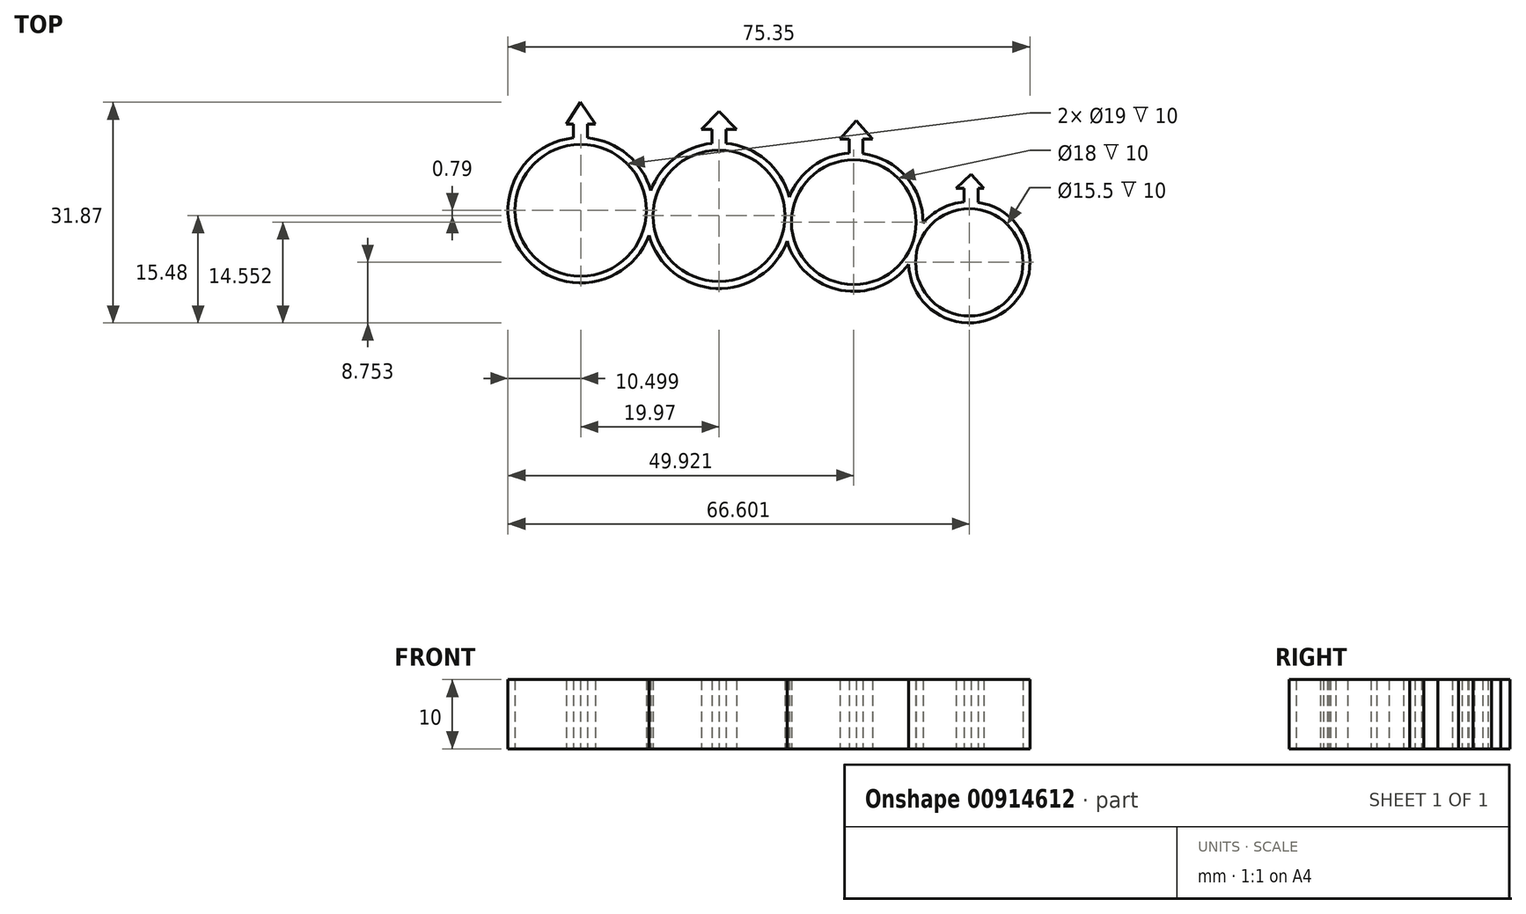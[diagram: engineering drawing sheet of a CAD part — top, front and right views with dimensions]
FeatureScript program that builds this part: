
annotation { "Feature Type Name" : "Feature", "Feature Type Description" : "" }
export const myFeature = defineFeature(function(context is Context, id is Id, definition is map)
    precondition{}
    {
        {
            var Q0;
            Q0=qCreatedBy(makeId("Top.planeOp"),FACE);
            var sketch = newSketch(context, id + "F0", { "sketchPlane" : qUnion([Q0])});
            skCircle(sketch, "E0", {"center": v(-63.63, 34.75) * mm, "radius": 9.5 * mm});
            skCircle(sketch, "E1", {"center": v(-43.66, 33.96) * mm, "radius": 9.5 * mm});
            skCircle(sketch, "E2", {"center": v(-24.2, 33.03) * mm, "radius": 9 * mm});
            skCircle(sketch, "E3", {"center": v(-7.53, 27.23) * mm, "radius": 7.75 * mm});
            skCircle(sketch, "E4", {"center": v(-63.63, 34.75) * mm, "radius": 10.5 * mm});
            skCircle(sketch, "E5", {"center": v(-43.66, 33.96) * mm, "radius": 10.5 * mm});
            skCircle(sketch, "E6", {"center": v(-24.2, 33.03) * mm, "radius": 10 * mm});
            skCircle(sketch, "E7", {"center": v(-7.53, 27.23) * mm, "radius": 8.75 * mm});
            skLineSegment(sketch, "E8", {"start": v(-64.68, 45.2) * mm, "end": v(-64.68, 47.2) * mm});
            skLineSegment(sketch, "E9", {"start": v(-64.68, 47.2) * mm, "end": v(-62.68, 47.2) * mm});
            skLineSegment(sketch, "E10", {"start": v(-62.68, 47.2) * mm, "end": v(-62.68, 45.2) * mm});
            skLineSegment(sketch, "E11", {"start": v(-44.67, 44.41) * mm, "end": v(-44.67, 46.41) * mm});
            skLineSegment(sketch, "E12", {"start": v(-44.67, 46.41) * mm, "end": v(-42.67, 46.41) * mm});
            skLineSegment(sketch, "E13", {"start": v(-42.67, 46.41) * mm, "end": v(-42.67, 44.41) * mm});
            skLineSegment(sketch, "E14", {"start": v(-42.67, 44.41) * mm, "end": v(-42.67, 46.41) * mm});
            skLineSegment(sketch, "E15", {"start": v(-24.87, 43) * mm, "end": v(-24.87, 45) * mm});
            skLineSegment(sketch, "E16", {"start": v(-24.87, 45) * mm, "end": v(-22.87, 45.07) * mm});
            skLineSegment(sketch, "E17", {"start": v(-22.87, 45.07) * mm, "end": v(-22.87, 42.94) * mm});
            skLineSegment(sketch, "E18", {"start": v(-22.87, 42.94) * mm, "end": v(-22.87, 45.07) * mm});
            skLineSegment(sketch, "E19", {"start": v(-8.27, 35.95) * mm, "end": v(-8.27, 37.95) * mm});
            skLineSegment(sketch, "E20", {"start": v(-8.27, 37.95) * mm, "end": v(-6.27, 37.95) * mm});
            skLineSegment(sketch, "E21", {"start": v(-6.27, 37.95) * mm, "end": v(-6.27, 35.9) * mm});
            skLineSegment(sketch, "E22", {"start": v(-64.68, 47.2) * mm, "end": v(-65.72, 47.2) * mm});
            skLineSegment(sketch, "E23", {"start": v(-65.72, 47.2) * mm, "end": v(-63.68, 50.35) * mm});
            skPoint(sketch, "E23.endSnap0", {"position": v(-63.68, 47.2) * mm});
            skLineSegment(sketch, "E24", {"start": v(-63.68, 50.35) * mm, "end": v(-61.49, 47.2) * mm});
            skLineSegment(sketch, "E25", {"start": v(-61.49, 47.2) * mm, "end": v(-62.68, 47.2) * mm});
            skLineSegment(sketch, "E26", {"start": v(-44.67, 46.41) * mm, "end": v(-46.2, 46.41) * mm});
            skLineSegment(sketch, "E27", {"start": v(-46.2, 46.41) * mm, "end": v(-43.67, 49.02) * mm});
            skPoint(sketch, "E27.endSnap0", {"position": v(-43.67, 46.41) * mm});
            skLineSegment(sketch, "E28", {"start": v(-43.67, 49.02) * mm, "end": v(-41.14, 46.41) * mm});
            skLineSegment(sketch, "E29", {"start": v(-41.14, 46.41) * mm, "end": v(-42.67, 46.41) * mm});
            skLineSegment(sketch, "E30", {"start": v(-24.87, 45) * mm, "end": v(-26.2, 45) * mm});
            skLineSegment(sketch, "E31", {"start": v(-26.2, 45) * mm, "end": v(-23.87, 47.7) * mm});
            skPoint(sketch, "E31.endSnap0", {"position": v(-23.87, 45.04) * mm});
            skLineSegment(sketch, "E32", {"start": v(-23.87, 47.7) * mm, "end": v(-21.48, 45) * mm});
            skLineSegment(sketch, "E33", {"start": v(-21.48, 45) * mm, "end": v(-22.87, 45.07) * mm});
            skLineSegment(sketch, "E34", {"start": v(-8.27, 37.95) * mm, "end": v(-9.45, 37.95) * mm});
            skLineSegment(sketch, "E35", {"start": v(-9.45, 37.95) * mm, "end": v(-7.27, 39.94) * mm});
            skPoint(sketch, "E35.endSnap0", {"position": v(-7.27, 37.95) * mm});
            skLineSegment(sketch, "E36", {"start": v(-7.27, 39.94) * mm, "end": v(-5.46, 37.95) * mm});
            skLineSegment(sketch, "E37", {"start": v(-5.46, 37.95) * mm, "end": v(-6.27, 37.95) * mm});
            skSolve(sketch);
        }
        {
            var Q0;
            Q0=qSketchRegion(id+"F0",true);
            extrude(context, id + "F1", {"entities" : qUnion([Q0]), "depth" : 10 * mm, "offsetDistance" : 25.4 * mm});
        }
    });
